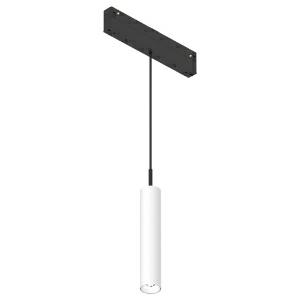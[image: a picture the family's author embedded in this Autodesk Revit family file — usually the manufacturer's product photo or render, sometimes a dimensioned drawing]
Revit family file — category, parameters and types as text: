
# Revit family: 2look4_25_magtrack_hangover_plug_o30_l150_insert_led_7w__2700k__48v__cri90_810-0410_8836
name_source: partatom
category: Leuchten
revit_build: Autodesk Revit 2016 (Build: 20190508_0715(x64)
units: mm (PartAtom-declared; Revit-internal decimal feet)

## family parameters
Basisbauteil = Fläche
Beim Laden mit Abzugskörper schneiden = Nein
Bemaßung runder Anschluss = Durchmesser verwenden
Gemeinsam genutzt = Nein
Lichtquelle = Nein
Raumberechnungspunkt = Nein
Teiletyp = Normal

## types (1)
- 810-0410-K24 (1 x LED, 448.11 lm, 6.4 W, 2700K)
    Beschreibung = The spot-insert 2LOOK4 25 MAGTRACK / 2LOOK4 50 MAGTRACK / HYPRO from the familiy 2LOOK4 consists of aluminum. The ballast is integrated and allows for an operation with 48V. 2LOOK4 25 MAGTRACK / 2LOOK4 50 MAGTRACK / HYPRO (# 810-0410) ist not dimmable (on/off). The lens based solution shows clear limits and creates sharp contours.
    CIE Flux Codes = 99 100 100 100 74
    Color Rendering = 1A/90…99
    Color Temperature = 2700K
    Height = 0 mm  [stored 0 ft]
    Hersteller = Prolicht
    Lamp Light Flux = 448.11 lm
    Lamp Power = 6.4 W
    Lamp count = 1
    Lampe = 1 x LED
    Length = 28 mm
    Luminous efficacy = 52 lm/W
    ModVariant = Nein
    Modell = 810-0410
    Mounting Place = Ceiling
    Mounting Type = Recessed
    Number of Poles = 1
    OnlyDefault = Ja
    Power Factor = 1
    Product Name = 2LOOK4 25 MAGTRACK__HANGOVER PLUG Ø30 L150 insert LED 7W  2700K  48V  CRI90
    Product group = Trimless recessed profile systems
    ProductGroupID = 414
    Protection Class = Protection class
    Protection Degree = Degree of protection
    RLX_Detail_Level = 1
    RlxData = <blob elided: 38913 chars, md5=ceaebd15>
    Scheinlast = 6 VA
    Socket = socket
    Standby Power = 0 W
    System Light Flux = 331 lm
    System Power = 6 W
    Typenbild = 810-0410.jpg
    URL = http://relux.com
    VarID = 810-0410-k24
    Voltage = 0 V
    Vorgabe-Ansicht = 1800 mm
    Weight = 0.00 kg
    Width = 0 mm  [stored 0 ft]

note: [stored X ft] marks values corroborated as IEEE doubles in the binary element streams (Revit-internal decimal feet)

## geometry (parser evidence)
native form markers: Sweep x11
no freeform markers — native parametric forms only
